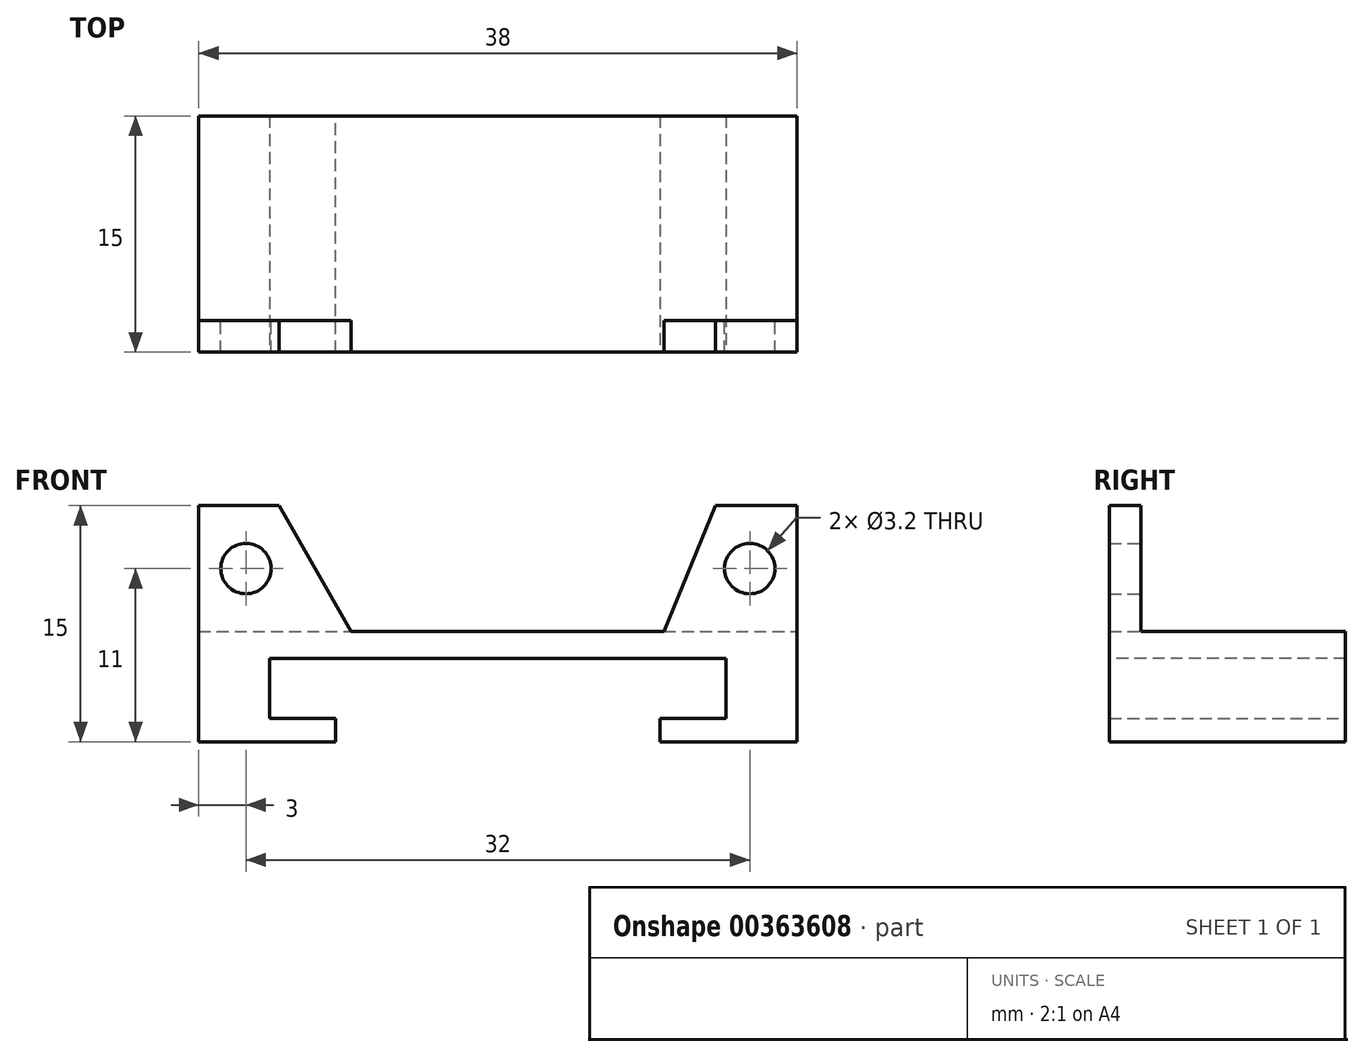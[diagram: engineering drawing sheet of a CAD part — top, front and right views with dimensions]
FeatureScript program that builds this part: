
annotation { "Feature Type Name" : "Feature", "Feature Type Description" : "" }
export const myFeature = defineFeature(function(context is Context, id is Id, definition is map)
    precondition{}
    {
        {
            var Q0;
            Q0=qCreatedBy(makeId("Top.planeOp"),FACE);
            var sketch = newSketch(context, id + "F0", { "sketchPlane" : qUnion([Q0])});
            skLineSegment(sketch, "E0.bottom", {"start": v(19, -7.5) * mm, "end": v(-19, -7.5) * mm});
            skLineSegment(sketch, "E0.top", {"start": v(19, 7.5) * mm, "end": v(-19, 7.5) * mm});
            skLineSegment(sketch, "E0.left", {"start": v(19, -7.5) * mm, "end": v(19, 7.5) * mm});
            skLineSegment(sketch, "E0.right", {"start": v(-19, -7.5) * mm, "end": v(-19, 7.5) * mm});
            skPoint(sketch, "E0.middle", {"position": v(0, 0) * mm});
            skSolve(sketch);
        }
        {
            var Q0;
            Q0=makeQuery(id+"F0.imprint","IMPRINT",FACE,{"disambiguationData":[TD([[makeQuery(id+"F0.imprint","IMPRINT",EDGE,{"derivedFrom":sQuery(id+"F0.wireOp",EDGE,"E0.bottom")}),-1.0]])]});
            extrude(context, id + "F1", {"entities" : qUnion([Q0]), "depth" : 7 * mm});
        }
        {
            var Q0;
            Q0=makeQuery(id+"F1.opExtrude","SWEPT_FACE",FACE,{"disambiguationData":[OSD([sQuery(id+"F0.wireOp",EDGE,"E0.bottom")])]});
            var sketch = newSketch(context, id + "F2", { "sketchPlane" : qUnion([Q0])});
            skLineSegment(sketch, "E1.bottom", {"start": v(14.5, 1.5) * mm, "end": v(-14.5, 1.5) * mm});
            skLineSegment(sketch, "E1.top", {"start": v(14.5, 5.3) * mm, "end": v(-14.5, 5.3) * mm});
            skLineSegment(sketch, "E1.left", {"start": v(14.5, 1.5) * mm, "end": v(14.5, 5.3) * mm});
            skLineSegment(sketch, "E1.right", {"start": v(-14.5, 1.5) * mm, "end": v(-14.5, 5.3) * mm});
            skPoint(sketch, "E1.middle", {"position": v(0, 3.4) * mm});
            skSolve(sketch);
        }
        {
            var Q0;
            Q0=makeQuery(id+"F2.imprint","IMPRINT",FACE,{"disambiguationData":[TD([[makeQuery(id+"F2.imprint","IMPRINT",EDGE,{"derivedFrom":sQuery(id+"F2.wireOp",EDGE,"E1.bottom")}),-1.0]])]});
            extrude(context, id + "F3", {"entities" : qUnion([Q0]), "operationType" : NewBodyOperationType.REMOVE, "oppositeDirection" : true, "depth" : 30 * mm});
        }
        {
            var Q0;
            Q0=makeQuery(id+"F1.opExtrude","CAP_FACE",FACE,{"disambiguationData":[OSD([sQuery(id+"F0.wireOp",EDGE,"E0.bottom"),sQuery(id+"F0.wireOp",EDGE,"E0.top"),sQuery(id+"F0.wireOp",EDGE,"E0.left"),sQuery(id+"F0.wireOp",EDGE,"E0.right")])],"isStart":false});
            var sketch = newSketch(context, id + "F4", { "sketchPlane" : qUnion([Q0])});
            skLineSegment(sketch, "E2.bottom", {"start": v(-19, -7.5) * mm, "end": v(19, -7.5) * mm});
            skLineSegment(sketch, "E2.top", {"start": v(-19, -5.5) * mm, "end": v(19, -5.5) * mm});
            skLineSegment(sketch, "E2.left", {"start": v(-19, -7.5) * mm, "end": v(-19, -5.5) * mm});
            skLineSegment(sketch, "E2.right", {"start": v(19, -7.5) * mm, "end": v(19, -5.5) * mm});
            skSolve(sketch);
        }
        {
            var Q0;
            Q0=makeQuery(id+"F1.opExtrude","CAP_FACE",FACE,{"disambiguationData":[OSD([sQuery(id+"F0.wireOp",EDGE,"E0.bottom"),sQuery(id+"F0.wireOp",EDGE,"E0.top"),sQuery(id+"F0.wireOp",EDGE,"E0.left"),sQuery(id+"F0.wireOp",EDGE,"E0.right")])],"isStart":true});
            var sketch = newSketch(context, id + "F5", { "sketchPlane" : qUnion([Q0])});
            skLineSegment(sketch, "E3.bottom", {"start": v(10.3, -9.2) * mm, "end": v(-10.3, -9.2) * mm});
            skLineSegment(sketch, "E3.top", {"start": v(10.3, 9.2) * mm, "end": v(-10.3, 9.2) * mm});
            skLineSegment(sketch, "E3.left", {"start": v(10.3, -9.2) * mm, "end": v(10.3, 9.2) * mm});
            skLineSegment(sketch, "E3.right", {"start": v(-10.3, -9.2) * mm, "end": v(-10.3, 9.2) * mm});
            skPoint(sketch, "E3.middle", {"position": v(0, 0) * mm});
            skSolve(sketch);
        }
        {
            var Q0;
            {var subQ0=sQuery(id+"F5.wireOp",EDGE,"E3.left");var subQ1=makeQuery(id+"F1.opExtrude","CAP_EDGE",EDGE,{"disambiguationData":[OSD([sQuery(id+"F0.wireOp",EDGE,"E0.top")])],"isStart":true});var subQ2=makeQuery(id+"F5.imprint","INTERSECT",VERTEX,{"derivedFrom":[subQ1,subQ0]});Q0=makeQuery(id+"F5.imprint","IMPRINT",FACE,{"disambiguationData":[TD([[makeQuery(id+"F5.imprint","IMPRINT",EDGE,{"disambiguationData":[TD([[subQ2,-1.0]])],"derivedFrom":subQ0}),1.0]])]});}
            extrude(context, id + "F6", {"entities" : qUnion([Q0]), "operationType" : NewBodyOperationType.REMOVE, "oppositeDirection" : true, "depth" : 5 * mm});
        }
        {
            var Q0;
            Q0=makeQuery(id+"F4.imprint","IMPRINT",FACE,{"disambiguationData":[TD([[makeQuery(id+"F4.imprint","IMPRINT",EDGE,{"derivedFrom":sQuery(id+"F4.wireOp",EDGE,"E2.bottom")}),-1.0]])]});
            extrude(context, id + "F7", {"entities" : qUnion([Q0]), "operationType" : NewBodyOperationType.ADD, "depth" : 8 * mm});
        }
        {
            var Q0;
            Q0=makeQuery(id+"F7.opExtrude","SWEPT_FACE",FACE,{"disambiguationData":[OSD([sQuery(id+"F4.wireOp",EDGE,"E2.top")])]});
            var sketch = newSketch(context, id + "F8", { "sketchPlane" : qUnion([Q0])});
            skPoint(sketch, "E4", {"position": v(16, 11) * mm});
            skPoint(sketch, "E4.positionSnap0", {"position": v(19, 11) * mm});
            skPoint(sketch, "E5", {"position": v(-16, 11) * mm});
            skLineSegment(sketch, "E6", {"start": v(14.23, 15.62) * mm, "end": v(9.33, 7) * mm});
            skLineSegment(sketch, "E7", {"start": v(-10.54, 7) * mm, "end": v(-14.65, 17.03) * mm});
            skSolve(sketch);
        }
        {
            var Q0;
            Q0=sQuery(id+"F8.wireOp",VERTEX,"E4");
            var Q1;
            Q1=sQuery(id+"F8.wireOp",VERTEX,"E5");
            var Q2;
            Q2=makeQuery(id+"F1.opExtrude","SWEPT_BODY",BODY,{"disambiguationData":[OSD([sQuery(id+"F0.wireOp",EDGE,"E0.bottom"),sQuery(id+"F0.wireOp",EDGE,"E0.top"),sQuery(id+"F0.wireOp",EDGE,"E0.left"),sQuery(id+"F0.wireOp",EDGE,"E0.right")])]});
            hole(context, id + "F9", {"style" : HoleStyle.SIMPLE, "endStyle" : HoleEndStyle.THROUGH, "holeDiameter" : 3.2 * mm, "tappedDepth" : 12 * mm, "tapClearance" : 3, "locations" : qUnion([Q0, Q1]), "scope" : qUnion([Q2])});
        }
        {
            var Q0;
            {var subQ0=sQuery(id+"F8.wireOp",EDGE,"E6");var subQ1=sQuery(id+"F4.wireOp",EDGE,"E2.top");var subQ2=makeQuery(id+"F7.opExtrude","CAP_EDGE",EDGE,{"disambiguationData":[OSD([subQ1])],"isStart":true});var subQ3=makeQuery(id+"F8.imprint","INTERSECT",VERTEX,{"derivedFrom":[subQ2,subQ0]});Q0=makeQuery(id+"F8.imprint","IMPRINT",FACE,{"disambiguationData":[TD([[makeQuery(id+"F8.imprint","IMPRINT",EDGE,{"disambiguationData":[TD([[subQ3,1.0]])],"derivedFrom":subQ0}),-1.0]])]});}
            extrude(context, id + "F10", {"entities" : qUnion([Q0]), "operationType" : NewBodyOperationType.REMOVE, "oppositeDirection" : true, "depth" : 25 * mm});
        }
    });
